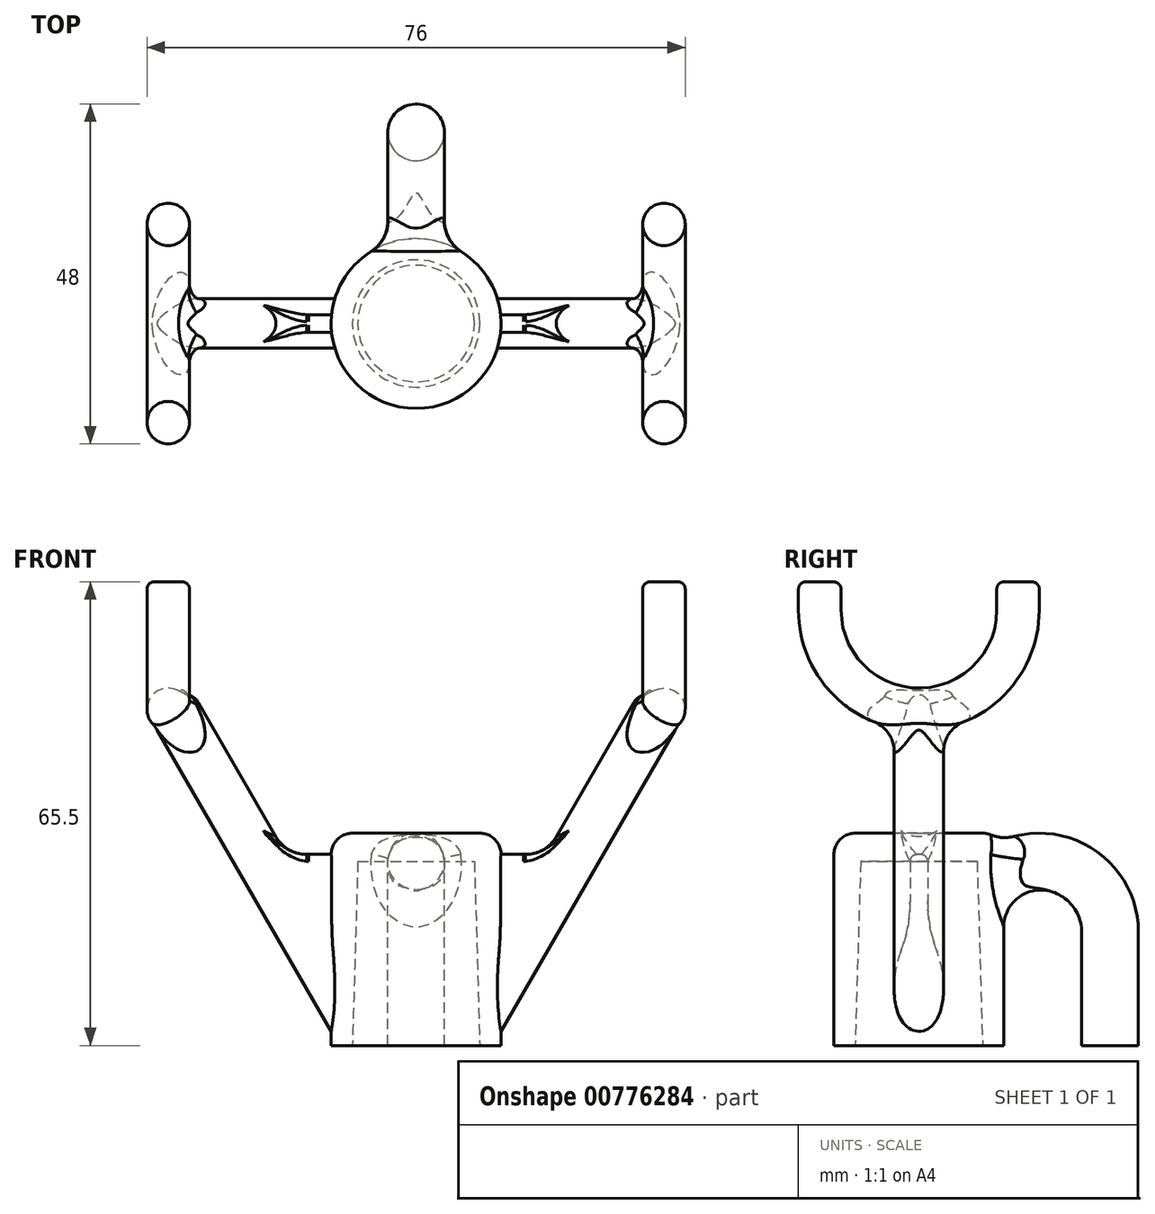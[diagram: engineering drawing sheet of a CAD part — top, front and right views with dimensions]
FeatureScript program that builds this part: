
annotation { "Feature Type Name" : "Feature", "Feature Type Description" : "" }
export const myFeature = defineFeature(function(context is Context, id is Id, definition is map)
    precondition{}
    {
        {
            var Q0;
            Q0=qCreatedBy(makeId("Top.planeOp"),FACE);
            var sketch = newSketch(context, id + "F0", { "sketchPlane" : qUnion([Q0])});
            skCircle(sketch, "E0", {"center": v(0, 0) * mm, "radius": 12 * mm});
            skSolve(sketch);
        }
        {
            var Q0;
            Q0=makeQuery(id+"F0.imprint","IMPRINT",FACE,{"disambiguationData":[TD([[makeQuery(id+"F0.imprint","IMPRINT",EDGE,{"derivedFrom":sQuery(id+"F0.wireOp",EDGE,"E0")}),1.0]])]});
            extrude(context, id + "F1", {"entities" : qUnion([Q0]), "depth" : 30 * mm, "offsetDistance" : 25 * mm});
        }
        {
            var Q0;
            Q0=qCreatedBy(makeId("Right.planeOp"),FACE);
            var sketch = newSketch(context, id + "F2", { "sketchPlane" : qUnion([Q0])});
            skLineSegment(sketch, "E1", {"start": v(27, 0) * mm, "end": v(27, 16) * mm});
            skArc(sketch, "E2", {"start": v(27, 16) * mm, "mid": v(17.81, 25.97) * mm, "end": v(7.13, 17.62) * mm});
            skSolve(sketch);
        }
        {
            var Q0;
            Q0=qCreatedBy(makeId("Top.planeOp"),FACE);
            var sketch = newSketch(context, id + "F3", { "sketchPlane" : qUnion([Q0])});
            skCircle(sketch, "E3", {"center": v(0, 27) * mm, "radius": 4 * mm});
            skSolve(sketch);
        }
        {
            var Q0;
            Q0=makeQuery(id+"F1.opExtrude","CAP_FACE",FACE,{"disambiguationData":[OSD([sQuery(id+"F0.wireOp",EDGE,"E0")])],"isStart":false});
            fillet(context, id + "F4", {"entities" : qUnion([Q0]), "radius" : 3 * mm, "tangentPropagation" : true, "allowEdgeOverflow" : false});
        }
        {
            var Q0;
            Q0=makeQuery(id+"F3.imprint","IMPRINT",FACE,{"disambiguationData":[TD([[makeQuery(id+"F3.imprint","IMPRINT",EDGE,{"derivedFrom":sQuery(id+"F3.wireOp",EDGE,"E3")}),1.0]])]});
            var Q1;
            Q1=sQuery(id+"F2.wireOp",EDGE,"E1");
            var Q2;
            Q2=sQuery(id+"F2.wireOp",EDGE,"E2");
            sweep(context, id + "F5", {"operationType" : NewBodyOperationType.ADD, "profiles" : qUnion([Q0]), "path" : qUnion([Q1, Q2])});
        }
        {
            var Q0;
            Q0=qCreatedBy(makeId("Front.planeOp"),FACE);
            var sketch = newSketch(context, id + "F6", { "sketchPlane" : qUnion([Q0])});
            skLineSegment(sketch, "E4", {"start": v(6.8, 0) * mm, "end": v(35, 48.84) * mm});
            skSolve(sketch);
        }
        {
            var Q0;
            Q0=sQuery(id+"F6.wireOp",VERTEX,"E4.end");
            var Q1;
            Q1=sQuery(id+"F6.wireOp",EDGE,"E4");
            cPlane(context, id + "F7", {"entities" : qUnion([Q0, Q1]), "cplaneType" : CPlaneType.LINE_POINT, "offset" : 25 * mm, "width" : 150 * mm, "height" : 150 * mm});
        }
        {
            var Q0;
            Q0=qCreatedBy(id+"F7.planeOp",FACE);
            var sketch = newSketch(context, id + "F8", { "sketchPlane" : qUnion([Q0])});
            skCircle(sketch, "E5", {"center": v(5.9, 0) * mm, "radius": 3.5 * mm});
            skSolve(sketch);
        }
        {
            var Q0;
            Q0=makeQuery(id+"F8.imprint","IMPRINT",FACE,{"disambiguationData":[TD([[makeQuery(id+"F8.imprint","IMPRINT",EDGE,{"derivedFrom":sQuery(id+"F8.wireOp",EDGE,"E5")}),1.0]])]});
            var Q1;
            Q1=makeQuery(id+"F1.opExtrude","SWEPT_BODY",BODY,{"disambiguationData":[OSD([sQuery(id+"F0.wireOp",EDGE,"E0")])]});
            extrude(context, id + "F9", {"entities" : qUnion([Q0]), "endBound" : BoundingType.UP_TO_BODY, "oppositeDirection" : true, "depth" : 54.3 * mm, "endBoundEntityBody" : qUnion([Q1]), "offsetDistance" : 25 * mm});
        }
        {
            var Q0;
            Q0=makeQuery(id+"F9.opExtrude","CAP_EDGE",EDGE,{"disambiguationData":[OSD([sQuery(id+"F8.wireOp",EDGE,"E5")])],"isStart":true});
            fillet(context, id + "F10", {"entities" : qUnion([Q0]), "radius" : 2.5 * mm, "tangentPropagation" : true, "allowEdgeOverflow" : false});
        }
        {
            var Q0;
            Q0=sQuery(id+"F6.wireOp",VERTEX,"E4.end");
            var Q1;
            Q1=qCreatedBy(makeId("Right.planeOp"),FACE);
            cPlane(context, id + "F11", {"entities" : qUnion([Q0, Q1]), "cplaneType" : CPlaneType.PLANE_POINT, "offset" : 25 * mm, "width" : 150 * mm, "height" : 150 * mm});
        }
        {
            var Q0;
            Q0=qCreatedBy(id+"F11.planeOp",FACE);
            var sketch = newSketch(context, id + "F12", { "sketchPlane" : qUnion([Q0])});
            skLineSegment(sketch, "E6", {"start": v(-14, 65.5) * mm, "end": v(-14, 61.5) * mm});
            skArc(sketch, "E7", {"start": v(-14, 61.5) * mm, "mid": v(0, 47.5) * mm, "end": v(14, 61.5) * mm});
            skLineSegment(sketch, "E8", {"start": v(14, 61.5) * mm, "end": v(14, 65.5) * mm});
            skSolve(sketch);
        }
        {
            var Q0;
            Q0=qCreatedBy(makeId("Top.planeOp"),FACE);
            var Q1;
            Q1=sQuery(id+"F12.wireOp",VERTEX,"E6.start");
            cPlane(context, id + "F13", {"entities" : qUnion([Q0, Q1]), "cplaneType" : CPlaneType.PLANE_POINT, "offset" : 25 * mm, "width" : 150 * mm, "height" : 150 * mm});
        }
        {
            var Q0;
            Q0=qCreatedBy(id+"F13.planeOp",FACE);
            var sketch = newSketch(context, id + "F14", { "sketchPlane" : qUnion([Q0])});
            skCircle(sketch, "E9", {"center": v(35, -14) * mm, "radius": 3 * mm});
            skSolve(sketch);
        }
        {
            var Q0;
            Q0=makeQuery(id+"F14.imprint","IMPRINT",FACE,{"disambiguationData":[TD([[makeQuery(id+"F14.imprint","IMPRINT",EDGE,{"derivedFrom":sQuery(id+"F14.wireOp",EDGE,"E9")}),1.0]])]});
            var Q1;
            Q1=sQuery(id+"F12.wireOp",EDGE,"E6");
            var Q2;
            Q2=sQuery(id+"F12.wireOp",EDGE,"E7");
            var Q3;
            Q3=sQuery(id+"F12.wireOp",EDGE,"E8");
            sweep(context, id + "F15", {"operationType" : NewBodyOperationType.ADD, "profiles" : qUnion([Q0]), "path" : qUnion([Q1, Q2, Q3])});
        }
        {
            var Q0;
            Q0=makeQuery(id+"F15.boolean.opBoolean","INTERSECT",EDGE,{"derivedFrom":[makeQuery(id+"F9.opExtrude","SWEPT_FACE",FACE,{"disambiguationData":[OSD([sQuery(id+"F8.wireOp",EDGE,"E5")])]}),makeQuery(id+"F15.opSweep","SWEPT_FACE",FACE,{"disambiguationData":[OSD([sQuery(id+"F12.wireOp",EDGE,"E7"),sQuery(id+"F14.wireOp",EDGE,"E9")])]})]});
            fillet(context, id + "F16", {"entities" : qUnion([Q0]), "radius" : 6 * mm, "tangentPropagation" : true, "allowEdgeOverflow" : false});
        }
        {
            var Q0;
            Q0=makeQuery(id+"F15.opSweep","CAP_FACE",FACE,{"disambiguationData":[OSD([sQuery(id+"F12.wireOp",VERTEX,"E8.end"),sQuery(id+"F14.wireOp",EDGE,"E9")])],"isStart":false});
            var Q1;
            Q1=makeQuery(id+"F15.opSweep","CAP_FACE",FACE,{"disambiguationData":[OSD([sQuery(id+"F12.wireOp",VERTEX,"E6.start"),sQuery(id+"F14.wireOp",EDGE,"E9")])],"isStart":true});
            fillet(context, id + "F17", {"entities" : qUnion([Q0, Q1]), "radius" : 1 * mm, "tangentPropagation" : true, "allowEdgeOverflow" : false});
        }
        {
            var Q0;
            Q0=makeQuery(id+"F9.opExtrude","SWEPT_BODY",BODY,{"disambiguationData":[OSD([sQuery(id+"F8.wireOp",EDGE,"E5")])]});
            var Q1;
            Q1=qCreatedBy(makeId("Right.planeOp"),FACE);
            mirror(context, id + "F18", {"operationType" : NewBodyOperationType.ADD, "entities" : qUnion([Q0]), "mirrorPlane" : qUnion([Q1])});
        }
        {
            var Q0;
            Q0=qCreatedBy(makeId("Front.planeOp"),FACE);
            var sketch = newSketch(context, id + "F19", { "sketchPlane" : qUnion([Q0])});
            skLineSegment(sketch, "E10.bottom", {"start": v(18.5, 27) * mm, "end": v(-18.5, 27) * mm});
            skLineSegment(sketch, "E10.top", {"start": v(18.5, 14) * mm, "end": v(-18.5, 14) * mm});
            skLineSegment(sketch, "E10.left", {"start": v(18.5, 27) * mm, "end": v(18.5, 14) * mm});
            skLineSegment(sketch, "E10.right", {"start": v(-18.5, 27) * mm, "end": v(-18.5, 14) * mm});
            skPoint(sketch, "E10.middle", {"position": v(0, 20.5) * mm});
            skSolve(sketch);
        }
        {
            var Q0;
            Q0=makeQuery(id+"F19.imprint","IMPRINT",FACE,{"disambiguationData":[TD([[makeQuery(id+"F19.imprint","IMPRINT",EDGE,{"derivedFrom":sQuery(id+"F19.wireOp",EDGE,"E10.bottom")}),1.0]])]});
            extrude(context, id + "F20", {"entities" : qUnion([Q0]), "operationType" : NewBodyOperationType.ADD, "endBound" : BoundingType.SYMMETRIC, "depth" : 2.5 * mm, "offsetDistance" : 25 * mm});
        }
        {
            var Q0;
            Q0=makeQuery(id+"F1.opExtrude","CAP_FACE",FACE,{"disambiguationData":[OSD([sQuery(id+"F0.wireOp",EDGE,"E0")])],"isStart":true});
            var sketch = newSketch(context, id + "F21", { "sketchPlane" : qUnion([Q0])});
            skCircle(sketch, "E11", {"center": v(0, 0) * mm, "radius": 9 * mm});
            skSolve(sketch);
        }
        {
            var Q0;
            Q0=makeQuery(id+"F21.imprint","IMPRINT",FACE,{"disambiguationData":[TD([[makeQuery(id+"F21.imprint","IMPRINT",EDGE,{"derivedFrom":sQuery(id+"F21.wireOp",EDGE,"E11")}),1.0]])]});
            extrude(context, id + "F22", {"entities" : qUnion([Q0]), "operationType" : NewBodyOperationType.REMOVE, "oppositeDirection" : true, "depth" : 26 * mm, "offsetDistance" : 25 * mm, "hasDraft" : true, "draftAngle" : 1.7 * degree, "draftPullDirection" : true});
        }
        {
            var Q0;
            Q0=makeQuery(id+"F20.boolean.opBoolean","INTERSECT",EDGE,{"disambiguationData":[OD(1.0)],"derivedFrom":[makeQuery(id+"F18.opPattern","COPY",FACE,{"derivedFrom":makeQuery(id+"F9.opExtrude","SWEPT_FACE",FACE,{"disambiguationData":[OSD([sQuery(id+"F8.wireOp",EDGE,"E5")])]}),"instanceName":"1"}),makeQuery(id+"F20.opExtrude","CAP_FACE",FACE,{"disambiguationData":[OSD([sQuery(id+"F19.wireOp",EDGE,"E10.bottom"),sQuery(id+"F19.wireOp",EDGE,"E10.top"),sQuery(id+"F19.wireOp",EDGE,"E10.left"),sQuery(id+"F19.wireOp",EDGE,"E10.right")])],"isStart":false})]});
            var Q1;
            Q1=makeQuery(id+"F20.boolean.opBoolean","INTERSECT",EDGE,{"derivedFrom":[makeQuery(id+"F18.opPattern","COPY",FACE,{"derivedFrom":makeQuery(id+"F9.opExtrude","SWEPT_FACE",FACE,{"disambiguationData":[OSD([sQuery(id+"F8.wireOp",EDGE,"E5")])]}),"instanceName":"1"}),makeQuery(id+"F20.opExtrude","SWEPT_FACE",FACE,{"disambiguationData":[OSD([sQuery(id+"F19.wireOp",EDGE,"E10.bottom")])]})]});
            var Q2;
            Q2=makeQuery(id+"F20.boolean.opBoolean","INTERSECT",EDGE,{"disambiguationData":[OD(1.0)],"derivedFrom":[makeQuery(id+"F18.opPattern","COPY",FACE,{"derivedFrom":makeQuery(id+"F9.opExtrude","SWEPT_FACE",FACE,{"disambiguationData":[OSD([sQuery(id+"F8.wireOp",EDGE,"E5")])]}),"instanceName":"1"}),makeQuery(id+"F20.opExtrude","CAP_FACE",FACE,{"disambiguationData":[OSD([sQuery(id+"F19.wireOp",EDGE,"E10.bottom"),sQuery(id+"F19.wireOp",EDGE,"E10.top"),sQuery(id+"F19.wireOp",EDGE,"E10.left"),sQuery(id+"F19.wireOp",EDGE,"E10.right")])],"isStart":true})]});
            var Q3;
            Q3=makeQuery(id+"F20.boolean.opBoolean","INTERSECT",EDGE,{"disambiguationData":[OD(1.0)],"derivedFrom":[makeQuery(id+"F9.opExtrude","SWEPT_FACE",FACE,{"disambiguationData":[OSD([sQuery(id+"F8.wireOp",EDGE,"E5")])]}),makeQuery(id+"F20.opExtrude","CAP_FACE",FACE,{"disambiguationData":[OSD([sQuery(id+"F19.wireOp",EDGE,"E10.bottom"),sQuery(id+"F19.wireOp",EDGE,"E10.top"),sQuery(id+"F19.wireOp",EDGE,"E10.left"),sQuery(id+"F19.wireOp",EDGE,"E10.right")])],"isStart":false})]});
            var Q4;
            Q4=makeQuery(id+"F20.boolean.opBoolean","INTERSECT",EDGE,{"derivedFrom":[makeQuery(id+"F9.opExtrude","SWEPT_FACE",FACE,{"disambiguationData":[OSD([sQuery(id+"F8.wireOp",EDGE,"E5")])]}),makeQuery(id+"F20.opExtrude","SWEPT_FACE",FACE,{"disambiguationData":[OSD([sQuery(id+"F19.wireOp",EDGE,"E10.bottom")])]})]});
            var Q5;
            Q5=makeQuery(id+"F20.boolean.opBoolean","INTERSECT",EDGE,{"disambiguationData":[OD(1.0)],"derivedFrom":[makeQuery(id+"F9.opExtrude","SWEPT_FACE",FACE,{"disambiguationData":[OSD([sQuery(id+"F8.wireOp",EDGE,"E5")])]}),makeQuery(id+"F20.opExtrude","CAP_FACE",FACE,{"disambiguationData":[OSD([sQuery(id+"F19.wireOp",EDGE,"E10.bottom"),sQuery(id+"F19.wireOp",EDGE,"E10.top"),sQuery(id+"F19.wireOp",EDGE,"E10.left"),sQuery(id+"F19.wireOp",EDGE,"E10.right")])],"isStart":true})]});
            fillet(context, id + "F23", {"entities" : qUnion([Q0, Q1, Q2, Q3, Q4, Q5]), "radius" : 5 * mm, "tangentPropagation" : true, "allowEdgeOverflow" : false});
        }
        {
            var Q0;
            {var subQ0=sQuery(id+"F19.wireOp",EDGE,"E10.bottom");Q0=makeQuery(id+"F20.boolean.opBoolean","SPLIT",EDGE,{"disambiguationData":[TD([makeQuery(id+"F18.opPattern","COPY",FACE,{"derivedFrom":makeQuery(id+"F9.opExtrude","SWEPT_FACE",FACE,{"disambiguationData":[OSD([sQuery(id+"F8.wireOp",EDGE,"E5")])]}),"instanceName":"1"})])],"derivedFrom":makeQuery(id+"F20.opExtrude","CAP_EDGE",EDGE,{"disambiguationData":[OSD([subQ0])],"isStart":false})});}
            var Q1;
            {var subQ0=sQuery(id+"F19.wireOp",EDGE,"E10.bottom");var subQ1=makeQuery(id+"F18.opPattern","COPY",FACE,{"derivedFrom":makeQuery(id+"F9.opExtrude","SWEPT_FACE",FACE,{"disambiguationData":[OSD([sQuery(id+"F8.wireOp",EDGE,"E5")])]}),"instanceName":"1"});Q1=makeQuery(id+"F23.opFillet","BLEND_EDGE",EDGE,{"blendedFrom":[makeQuery(id+"F20.boolean.opBoolean","INTERSECT",EDGE,{"derivedFrom":[subQ1,makeQuery(id+"F20.opExtrude","SWEPT_FACE",FACE,{"disambiguationData":[OSD([subQ0])]})]}),makeQuery(id+"F20.boolean.opBoolean","INTERSECT",EDGE,{"disambiguationData":[OD(1.0)],"derivedFrom":[subQ1,makeQuery(id+"F20.opExtrude","CAP_FACE",FACE,{"disambiguationData":[OSD([subQ0,sQuery(id+"F19.wireOp",EDGE,"E10.top"),sQuery(id+"F19.wireOp",EDGE,"E10.left"),sQuery(id+"F19.wireOp",EDGE,"E10.right")])],"isStart":false})]})],"blendedInto":[]});}
            var Q2;
            {var subQ0=makeQuery(id+"F18.opPattern","COPY",FACE,{"derivedFrom":makeQuery(id+"F9.opExtrude","SWEPT_FACE",FACE,{"disambiguationData":[OSD([sQuery(id+"F8.wireOp",EDGE,"E5")])]}),"instanceName":"1"});var subQ1=sQuery(id+"F19.wireOp",EDGE,"E10.bottom");var subQ2=makeQuery(id+"F20.opExtrude","SWEPT_FACE",FACE,{"disambiguationData":[OSD([subQ1])]});Q2=makeQuery(id+"F23.opFillet","BLEND_EDGE",EDGE,{"blendedFrom":[makeQuery(id+"F20.boolean.opBoolean","INTERSECT",EDGE,{"derivedFrom":[subQ0,subQ2]}),makeQuery(id+"F20.boolean.opBoolean","SPLIT",FACE,{"disambiguationData":[TD([makeQuery(id+"F1.opExtrude","SWEPT_FACE",FACE,{"disambiguationData":[OSD([sQuery(id+"F0.wireOp",EDGE,"E0")])]}),subQ0,subQ2])],"derivedFrom":makeQuery(id+"F20.opExtrude","CAP_FACE",FACE,{"disambiguationData":[OSD([subQ1,sQuery(id+"F19.wireOp",EDGE,"E10.top"),sQuery(id+"F19.wireOp",EDGE,"E10.left"),sQuery(id+"F19.wireOp",EDGE,"E10.right")])],"isStart":false})})],"blendedInto":[makeQuery(id+"F20.boolean.opBoolean","SPLIT",FACE,{"disambiguationData":[TD([makeQuery(id+"F1.opExtrude","SWEPT_FACE",FACE,{"disambiguationData":[OSD([sQuery(id+"F0.wireOp",EDGE,"E0")])]}),subQ0,subQ2])],"derivedFrom":makeQuery(id+"F20.opExtrude","CAP_FACE",FACE,{"disambiguationData":[OSD([subQ1,sQuery(id+"F19.wireOp",EDGE,"E10.top"),sQuery(id+"F19.wireOp",EDGE,"E10.left"),sQuery(id+"F19.wireOp",EDGE,"E10.right")])],"isStart":false})})]});}
            var Q3;
            {var subQ0=sQuery(id+"F19.wireOp",EDGE,"E10.bottom");var subQ1=makeQuery(id+"F9.opExtrude","SWEPT_FACE",FACE,{"disambiguationData":[OSD([sQuery(id+"F8.wireOp",EDGE,"E5")])]});Q3=makeQuery(id+"F23.opFillet","BLEND_EDGE",EDGE,{"blendedFrom":[makeQuery(id+"F20.boolean.opBoolean","INTERSECT",EDGE,{"derivedFrom":[subQ1,makeQuery(id+"F20.opExtrude","SWEPT_FACE",FACE,{"disambiguationData":[OSD([subQ0])]})]}),makeQuery(id+"F20.boolean.opBoolean","INTERSECT",EDGE,{"disambiguationData":[OD(1.0)],"derivedFrom":[subQ1,makeQuery(id+"F20.opExtrude","CAP_FACE",FACE,{"disambiguationData":[OSD([subQ0,sQuery(id+"F19.wireOp",EDGE,"E10.top"),sQuery(id+"F19.wireOp",EDGE,"E10.left"),sQuery(id+"F19.wireOp",EDGE,"E10.right")])],"isStart":false})]})],"blendedInto":[]});}
            var Q4;
            {var subQ0=sQuery(id+"F19.wireOp",EDGE,"E10.bottom");var subQ1=makeQuery(id+"F18.opPattern","COPY",FACE,{"derivedFrom":makeQuery(id+"F9.opExtrude","SWEPT_FACE",FACE,{"disambiguationData":[OSD([sQuery(id+"F8.wireOp",EDGE,"E5")])]}),"instanceName":"1"});Q4=makeQuery(id+"F23.opFillet","BLEND_EDGE",EDGE,{"blendedFrom":[makeQuery(id+"F20.boolean.opBoolean","INTERSECT",EDGE,{"derivedFrom":[subQ1,makeQuery(id+"F20.opExtrude","SWEPT_FACE",FACE,{"disambiguationData":[OSD([subQ0])]})]}),makeQuery(id+"F20.boolean.opBoolean","INTERSECT",EDGE,{"disambiguationData":[OD(1.0)],"derivedFrom":[subQ1,makeQuery(id+"F20.opExtrude","CAP_FACE",FACE,{"disambiguationData":[OSD([subQ0,sQuery(id+"F19.wireOp",EDGE,"E10.top"),sQuery(id+"F19.wireOp",EDGE,"E10.left"),sQuery(id+"F19.wireOp",EDGE,"E10.right")])],"isStart":true})]})],"blendedInto":[]});}
            var Q5;
            {var subQ0=sQuery(id+"F19.wireOp",EDGE,"E10.bottom");Q5=makeQuery(id+"F20.boolean.opBoolean","SPLIT",EDGE,{"disambiguationData":[TD([makeQuery(id+"F9.opExtrude","SWEPT_FACE",FACE,{"disambiguationData":[OSD([sQuery(id+"F8.wireOp",EDGE,"E5")])]})])],"derivedFrom":makeQuery(id+"F20.opExtrude","CAP_EDGE",EDGE,{"disambiguationData":[OSD([subQ0])],"isStart":true})});}
            var Q6;
            {var subQ0=sQuery(id+"F19.wireOp",EDGE,"E10.left");var subQ1=sQuery(id+"F19.wireOp",EDGE,"E10.bottom");Q6=makeQuery(id+"F20.boolean.opBoolean","SPLIT",EDGE,{"disambiguationData":[TD([makeQuery(id+"F20.opExtrude","SWEPT_FACE",FACE,{"disambiguationData":[OSD([subQ0])]})])],"derivedFrom":makeQuery(id+"F20.opExtrude","CAP_EDGE",EDGE,{"disambiguationData":[OSD([subQ1])],"isStart":true})});}
            fillet(context, id + "F24", {"entities" : qUnion([Q0, Q1, Q2, Q3, Q4, Q5, Q6]), "radius" : 1 * mm, "tangentPropagation" : true, "allowEdgeOverflow" : false});
        }
        {
            var Q0;
            Q0=makeQuery(id+"F5.boolean.opBoolean","INTERSECT",EDGE,{"derivedFrom":[makeQuery(id+"F1.opExtrude","SWEPT_FACE",FACE,{"disambiguationData":[OSD([sQuery(id+"F0.wireOp",EDGE,"E0")])]}),makeQuery(id+"F5.opSweep","SWEPT_FACE",FACE,{"disambiguationData":[OSD([sQuery(id+"F2.wireOp",EDGE,"E2"),sQuery(id+"F3.wireOp",EDGE,"E3")])]})]});
            fillet(context, id + "F25", {"entities" : qUnion([Q0]), "radius" : 5.2 * mm, "tangentPropagation" : true, "allowEdgeOverflow" : false});
        }
    });
